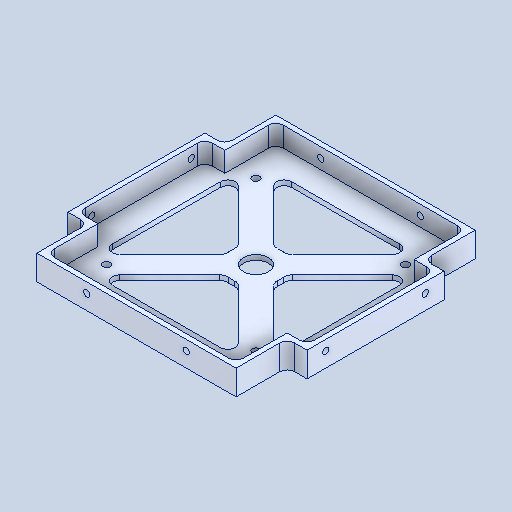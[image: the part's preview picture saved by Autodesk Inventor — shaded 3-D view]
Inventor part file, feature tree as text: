
AUTODESK INVENTOR PART (.ipt)
format: ipt  version: 2022 (Build 260153000, 153)  size: 194,560 bytes
history: mixed  units: in
note: dims shown in document units (in); Inventor stores cm internally (conversion verified against a paired STEP export)
features: mirror x1, imported_body x1
ambient origin geometry x8: Origin, YZ Plane, XZ Plane, XY Plane, X Axis, Y Axis, Z Axis, Center Point
bodies: Solid1 (imported_parasolid)
feature tree (2):
  mirror  "Mirror2"
  imported_body  NMx_Import_Brep_tag  [imported B-rep: ~84 faces, bbox_mm=[96.0, 10.0, 96.0]]
